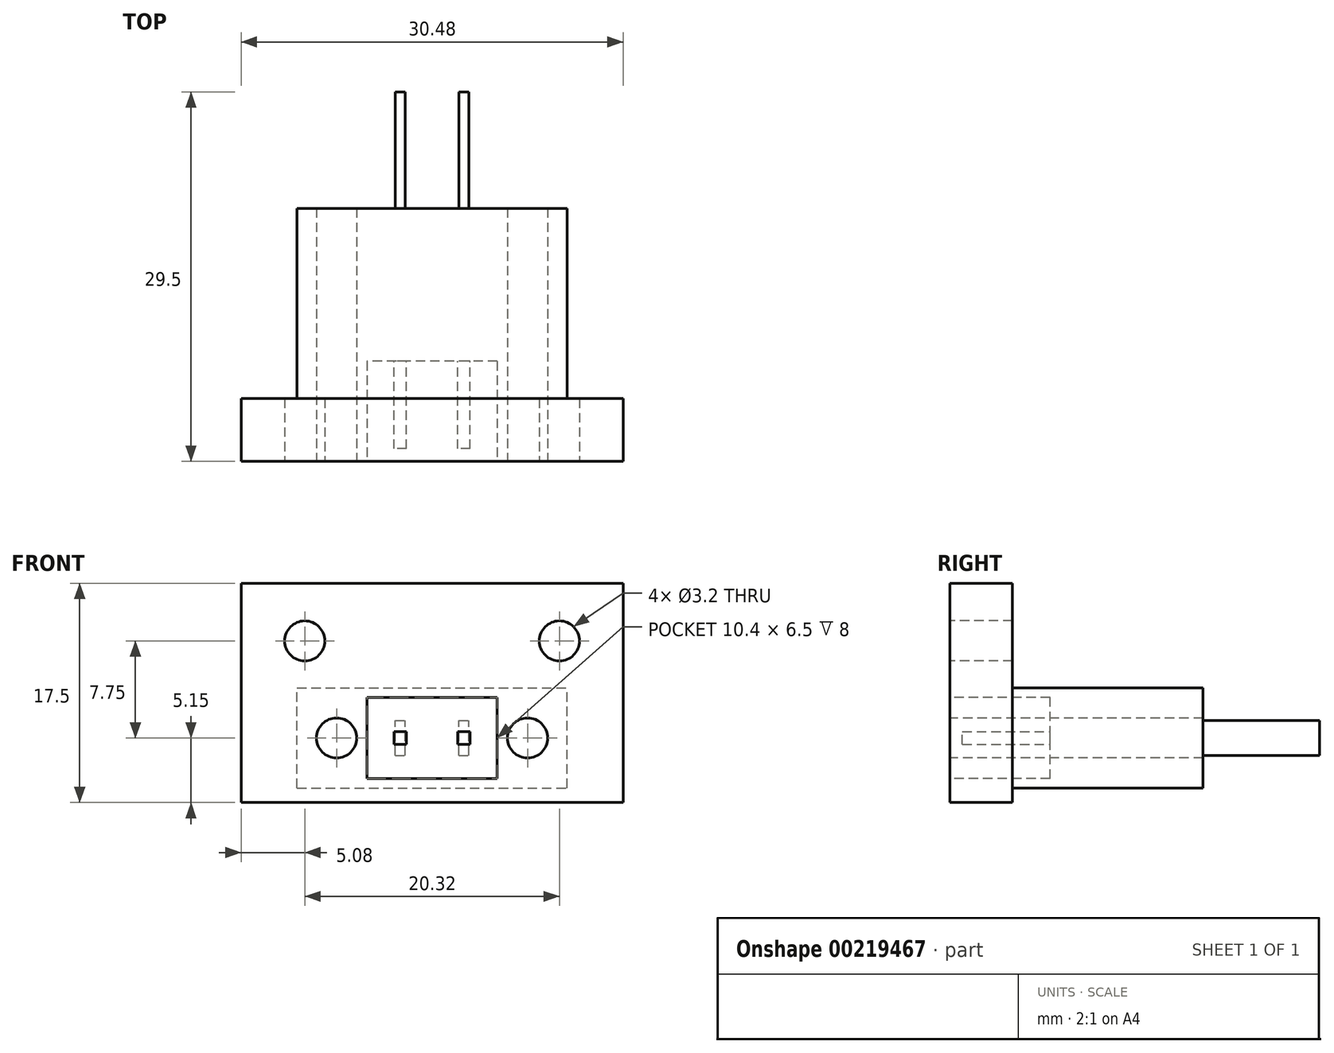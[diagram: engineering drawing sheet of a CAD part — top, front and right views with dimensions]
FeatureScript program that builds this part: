
annotation { "Feature Type Name" : "Feature", "Feature Type Description" : "" }
export const myFeature = defineFeature(function(context is Context, id is Id, definition is map)
    precondition{}
    {
        {
            var Q0;
            Q0=qCreatedBy(makeId("Front.planeOp"),FACE);
            var sketch = newSketch(context, id + "F0", { "sketchPlane" : qUnion([Q0])});
            skLineSegment(sketch, "E0.bottom", {"start": v(-15.24, -8.75) * mm, "end": v(15.24, -8.75) * mm});
            skLineSegment(sketch, "E0.top", {"start": v(-15.24, 8.75) * mm, "end": v(15.24, 8.75) * mm});
            skLineSegment(sketch, "E0.left", {"start": v(-15.24, -8.75) * mm, "end": v(-15.24, 8.75) * mm});
            skLineSegment(sketch, "E0.right", {"start": v(15.24, -8.75) * mm, "end": v(15.24, 8.75) * mm});
            skPoint(sketch, "E0.middle", {"position": v(0, 0) * mm});
            skSolve(sketch);
        }
        {
            var Q0;
            Q0=qSketchRegion(id+"F0",true);
            extrude(context, id + "F1", {"entities" : qUnion([Q0]), "depth" : 5 * mm});
        }
        {
            var Q0;
            Q0=makeQuery(id+"F1.opExtrude","CAP_FACE",FACE,{"disambiguationData":[OSD([sQuery(id+"F0.wireOp",EDGE,"E0.bottom"),sQuery(id+"F0.wireOp",EDGE,"E0.top"),sQuery(id+"F0.wireOp",EDGE,"E0.left"),sQuery(id+"F0.wireOp",EDGE,"E0.right")])],"isStart":false});
            var sketch = newSketch(context, id + "F2", { "sketchPlane" : qUnion([Q0])});
            skLineSegment(sketch, "E1.bottom", {"start": v(5.2, -6.85) * mm, "end": v(-5.2, -6.85) * mm});
            skLineSegment(sketch, "E1.top", {"start": v(5.2, -0.35) * mm, "end": v(-5.2, -0.35) * mm});
            skLineSegment(sketch, "E1.left", {"start": v(5.2, -6.85) * mm, "end": v(5.2, -0.35) * mm});
            skLineSegment(sketch, "E1.right", {"start": v(-5.2, -6.85) * mm, "end": v(-5.2, -0.35) * mm});
            skPoint(sketch, "E1.middle", {"position": v(0, -3.6) * mm});
            skSolve(sketch);
        }
        {
            var Q0;
            Q0=makeQuery(id+"F1.opExtrude","CAP_FACE",FACE,{"disambiguationData":[OSD([sQuery(id+"F0.wireOp",EDGE,"E0.bottom"),sQuery(id+"F0.wireOp",EDGE,"E0.top"),sQuery(id+"F0.wireOp",EDGE,"E0.left"),sQuery(id+"F0.wireOp",EDGE,"E0.right")])],"isStart":true});
            var sketch = newSketch(context, id + "F3", { "sketchPlane" : qUnion([Q0])});
            skLineSegment(sketch, "E2.bottom", {"start": v(10.78, -7.6) * mm, "end": v(-10.78, -7.6) * mm});
            skLineSegment(sketch, "E2.top", {"start": v(10.78, 0.4) * mm, "end": v(-10.78, 0.4) * mm});
            skLineSegment(sketch, "E2.left", {"start": v(10.78, -7.6) * mm, "end": v(10.78, 0.4) * mm});
            skLineSegment(sketch, "E2.right", {"start": v(-10.78, -7.6) * mm, "end": v(-10.78, 0.4) * mm});
            skPoint(sketch, "E2.middle", {"position": v(0, -3.6) * mm});
            skSolve(sketch);
        }
        {
            var Q0;
            Q0=qSketchRegion(id+"F3",true);
            extrude(context, id + "F4", {"entities" : qUnion([Q0]), "operationType" : NewBodyOperationType.ADD, "depth" : 15.2 * mm});
        }
        {
            var Q0;
            Q0=qSketchRegion(id+"F2",true);
            extrude(context, id + "F5", {"entities" : qUnion([Q0]), "operationType" : NewBodyOperationType.REMOVE, "oppositeDirection" : true, "depth" : 8 * mm});
        }
        {
            var Q0;
            Q0=makeQuery(id+"F1.opExtrude","CAP_FACE",FACE,{"disambiguationData":[OSD([sQuery(id+"F0.wireOp",EDGE,"E0.bottom"),sQuery(id+"F0.wireOp",EDGE,"E0.top"),sQuery(id+"F0.wireOp",EDGE,"E0.left"),sQuery(id+"F0.wireOp",EDGE,"E0.right")])],"isStart":false});
            var sketch = newSketch(context, id + "F6", { "sketchPlane" : qUnion([Q0])});
            skPoint(sketch, "E3", {"position": v(-10.16, 4.15) * mm});
            skPoint(sketch, "E4", {"position": v(10.16, 4.15) * mm});
            skPoint(sketch, "E5", {"position": v(-7.62, -3.6) * mm});
            skPoint(sketch, "E5.positionSnap0", {"position": v(-5.2, -3.6) * mm});
            skPoint(sketch, "E6", {"position": v(7.62, -3.6) * mm});
            skPoint(sketch, "E6.positionSnap0", {"position": v(5.2, -3.6) * mm});
            skSolve(sketch);
        }
        {
            var Q0;
            Q0=sQuery(id+"F6.wireOp",VERTEX,"E3");
            var Q1;
            Q1=sQuery(id+"F6.wireOp",VERTEX,"E5");
            var Q2;
            Q2=sQuery(id+"F6.wireOp",VERTEX,"E4");
            var Q3;
            Q3=sQuery(id+"F6.wireOp",VERTEX,"E6");
            var Q4;
            Q4=makeQuery(id+"F1.opExtrude","SWEPT_BODY",BODY,{"disambiguationData":[OSD([sQuery(id+"F0.wireOp",EDGE,"E0.bottom"),sQuery(id+"F0.wireOp",EDGE,"E0.top"),sQuery(id+"F0.wireOp",EDGE,"E0.left"),sQuery(id+"F0.wireOp",EDGE,"E0.right")])]});
            hole(context, id + "F7", {"style" : HoleStyle.SIMPLE, "endStyle" : HoleEndStyle.THROUGH, "holeDiameter" : 3.2 * mm, "startFromSketch" : true, "locations" : qUnion([Q0, Q1, Q2, Q3]), "scope" : qUnion([Q4]), "isTappedThrough" : true});
        }
        {
            var Q0;
            Q0=makeQuery(id+"F5.boolean.opBoolean","COPY",FACE,{"derivedFrom":makeQuery(id+"F5.opExtrude","CAP_FACE",FACE,{"disambiguationData":[OSD([sQuery(id+"F2.wireOp",EDGE,"E1.bottom"),sQuery(id+"F2.wireOp",EDGE,"E1.top"),sQuery(id+"F2.wireOp",EDGE,"E1.left"),sQuery(id+"F2.wireOp",EDGE,"E1.right")])],"isStart":false})});
            var sketch = newSketch(context, id + "F8", { "sketchPlane" : qUnion([Q0])});
            skLineSegment(sketch, "E7.bottom", {"start": v(3.04, -4.1) * mm, "end": v(2.04, -4.1) * mm});
            skLineSegment(sketch, "E7.top", {"start": v(3.04, -3.1) * mm, "end": v(2.04, -3.1) * mm});
            skLineSegment(sketch, "E7.left", {"start": v(3.04, -4.1) * mm, "end": v(3.04, -3.1) * mm});
            skLineSegment(sketch, "E7.right", {"start": v(2.04, -4.1) * mm, "end": v(2.04, -3.1) * mm});
            skPoint(sketch, "E7.middle", {"position": v(2.54, -3.6) * mm});
            skLineSegment(sketch, "E8.bottom", {"start": v(-2.04, -4.1) * mm, "end": v(-3.04, -4.1) * mm});
            skLineSegment(sketch, "E8.top", {"start": v(-2.04, -3.1) * mm, "end": v(-3.04, -3.1) * mm});
            skLineSegment(sketch, "E8.left", {"start": v(-2.04, -4.1) * mm, "end": v(-2.04, -3.1) * mm});
            skLineSegment(sketch, "E8.right", {"start": v(-3.04, -4.1) * mm, "end": v(-3.04, -3.1) * mm});
            skPoint(sketch, "E8.middle", {"position": v(-2.54, -3.6) * mm});
            skPoint(sketch, "E8.middle.positionSnap0", {"position": v(3.04, -3.6) * mm});
            skPoint(sketch, "E8.centerSnap0", {"position": v(3.04, -3.6) * mm});
            skPoint(sketch, "E9.middle.positionSnap0", {"position": v(-2.04, -3.6) * mm});
            skPoint(sketch, "E9.centerSnap0", {"position": v(-2.04, -3.6) * mm});
            skSolve(sketch);
        }
        {
            var Q0;
            Q0=qSketchRegion(id+"F8",true);
            extrude(context, id + "F9", {"entities" : qUnion([Q0]), "depth" : 7 * mm});
        }
        {
            var Q0;
            Q0=makeQuery(id+"F4.opExtrude","CAP_FACE",FACE,{"disambiguationData":[OSD([sQuery(id+"F3.wireOp",EDGE,"E2.bottom"),sQuery(id+"F3.wireOp",EDGE,"E2.top"),sQuery(id+"F3.wireOp",EDGE,"E2.left"),sQuery(id+"F3.wireOp",EDGE,"E2.right")])],"isStart":false});
            var sketch = newSketch(context, id + "F10", { "sketchPlane" : qUnion([Q0])});
            skPoint(sketch, "E10.middle.positionSnap0", {"position": v(-10.78, -3.6) * mm});
            skPoint(sketch, "E10.centerSnap0", {"position": v(-10.78, -3.6) * mm});
            skLineSegment(sketch, "E11.bottom", {"start": v(-2.13, -5) * mm, "end": v(-2.95, -5) * mm});
            skLineSegment(sketch, "E11.top", {"start": v(-2.13, -2.2) * mm, "end": v(-2.95, -2.2) * mm});
            skLineSegment(sketch, "E11.left", {"start": v(-2.13, -5) * mm, "end": v(-2.13, -2.2) * mm});
            skLineSegment(sketch, "E11.right", {"start": v(-2.95, -5) * mm, "end": v(-2.95, -2.2) * mm});
            skPoint(sketch, "E11.middle", {"position": v(-2.54, -3.6) * mm});
            skLineSegment(sketch, "E12.bottom", {"start": v(2.95, -5) * mm, "end": v(2.13, -5) * mm});
            skLineSegment(sketch, "E12.top", {"start": v(2.95, -2.2) * mm, "end": v(2.13, -2.2) * mm});
            skLineSegment(sketch, "E12.left", {"start": v(2.95, -5) * mm, "end": v(2.95, -2.2) * mm});
            skLineSegment(sketch, "E12.right", {"start": v(2.13, -5) * mm, "end": v(2.13, -2.2) * mm});
            skPoint(sketch, "E12.middle", {"position": v(2.54, -3.6) * mm});
            skPoint(sketch, "E12.middle.positionSnap0", {"position": v(-2.13, -3.6) * mm});
            skPoint(sketch, "E12.centerSnap0", {"position": v(-2.13, -3.6) * mm});
            skSolve(sketch);
        }
        {
            var Q0;
            Q0=qSketchRegion(id+"F10",true);
            extrude(context, id + "F11", {"entities" : qUnion([Q0]), "depth" : 9.3 * mm});
        }
    });
